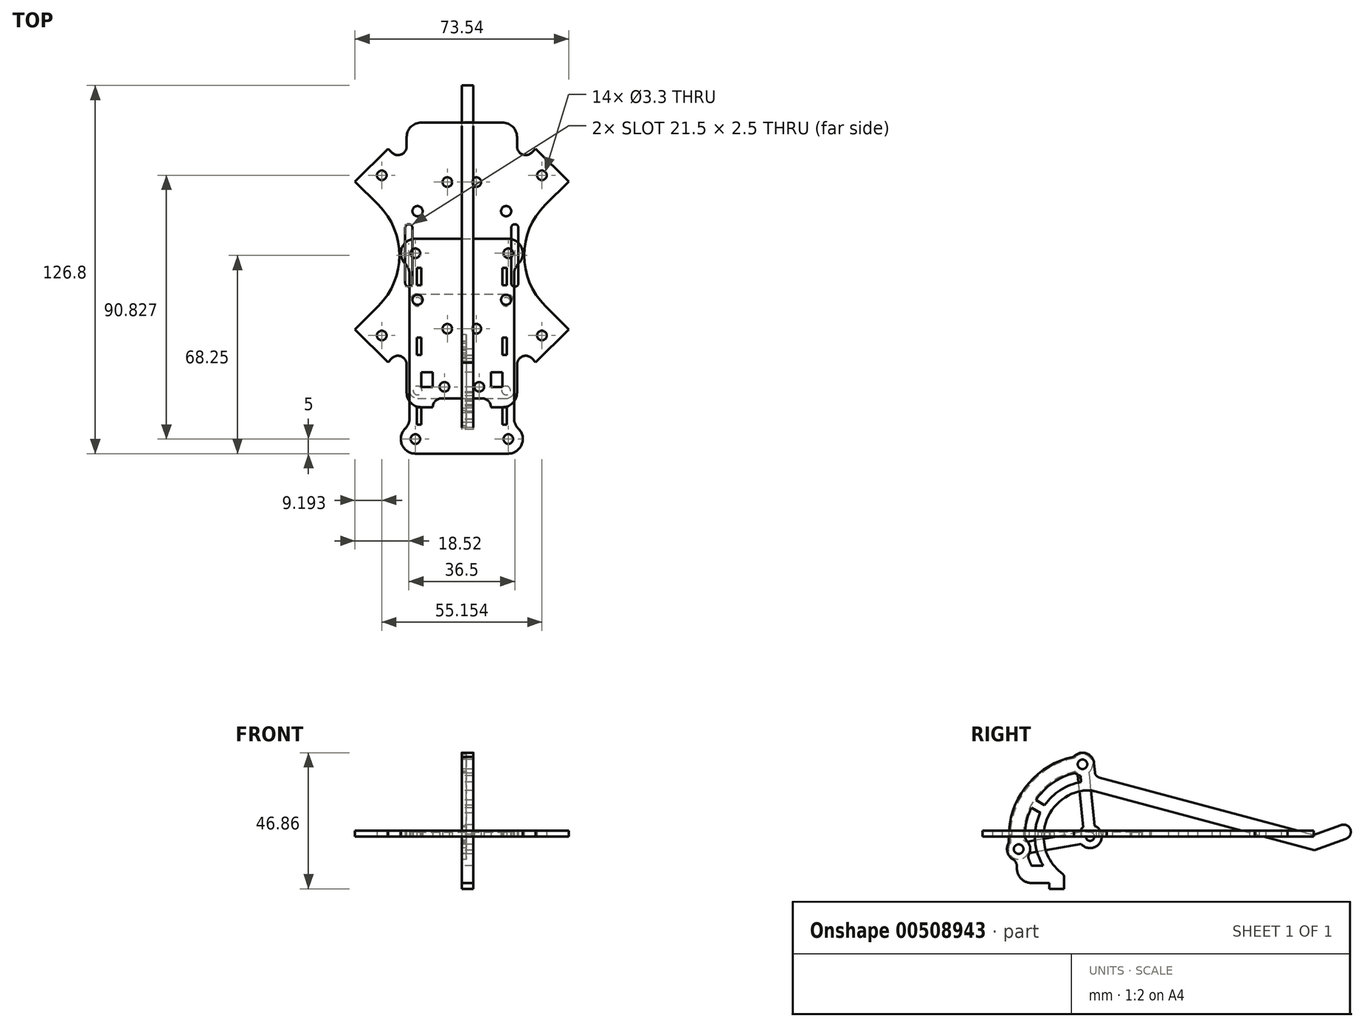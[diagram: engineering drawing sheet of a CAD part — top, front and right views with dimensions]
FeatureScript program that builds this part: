
annotation { "Feature Type Name" : "Feature", "Feature Type Description" : "" }
export const myFeature = defineFeature(function(context is Context, id is Id, definition is map)
    precondition{}
    {
        {
            var Q0;
            Q0=qCreatedBy(makeId("Right.planeOp"),FACE);
            var sketch = newSketch(context, id + "F0", { "sketchPlane" : qUnion([Q0])});
            skCircle(sketch, "E0", {"center": v(0, 0) * mm, "radius": 1.5 * mm, "construction": true});
            skArc(sketch, "E1", {"start": v(-5.7, 27.42) * mm, "mid": v(-22.11, 17.18) * mm, "end": v(-27.97, -1.26) * mm});
            skArc(sketch, "E2", {"start": v(-5.27, 21.87) * mm, "mid": v(-12.86, 18.46) * mm, "end": v(-18.7, 12.52) * mm});
            skLineSegment(sketch, "E3", {"start": v(0, 0) * mm, "end": v(-24.25, 14) * mm, "construction": true});
            skLineSegment(sketch, "E4", {"start": v(0, 0) * mm, "end": v(-60.65, 0) * mm, "construction": true});
            skLineSegment(sketch, "E5", {"start": v(0, 0) * mm, "end": v(-14.34, 20.48) * mm, "construction": true});
            skCircle(sketch, "E6", {"center": v(0, 0) * mm, "radius": 14 * mm, "construction": true});
            skLineSegment(sketch, "E7", {"start": v(-20.16, -10) * mm, "end": v(-16.16, -10) * mm});
            skArc(sketch, "E8", {"start": v(-12.49, -10) * mm, "mid": v(-11.05, -11.57) * mm, "end": v(-9.41, -12.94) * mm});
            skLineSegment(sketch, "E9.trimOffspring", {"start": v(-9, -16) * mm, "end": v(-9, -16) * mm});
            skPoint(sketch, "E10.visualSharp", {"position": v(-20.16, -10) * mm});
            skPoint(sketch, "E11.visualSharp", {"position": v(-22.98, -16) * mm});
            skArc(sketch, "E11.filletArc", {"start": v(-25.18, -10.6) * mm, "mid": v(-23.87, -14.4) * mm, "end": v(-20.2, -16) * mm});
            skLineSegment(sketch, "E12", {"start": v(-14, -16) * mm, "end": v(-14, -18) * mm});
            skLineSegment(sketch, "E13", {"start": v(-14, -18) * mm, "end": v(-9, -18) * mm});
            skLineSegment(sketch, "E14", {"start": v(-9, -18) * mm, "end": v(-9, -16) * mm});
            skLineSegment(sketch, "E15.trimOffspring", {"start": v(-14, -16) * mm, "end": v(-20.2, -16) * mm});
            skLineSegment(sketch, "E16", {"start": v(-9, -13.75) * mm, "end": v(-9, -16) * mm});
            skCircle(sketch, "E17", {"center": v(-24.62, -4.34) * mm, "radius": 1.65 * mm});
            skLineSegment(sketch, "E18", {"start": v(-24.62, -4.34) * mm, "end": v(0, 0) * mm, "construction": true});
            skArc(sketch, "E19", {"start": v(-28.25, -2.66) * mm, "mid": v(-28.44, -5.53) * mm, "end": v(-26.65, -7.79) * mm});
            skArc(sketch, "E20.trimOffspring", {"start": v(-21.45, -6.78) * mm, "mid": v(-20.62, -4.16) * mm, "end": v(-21.7, -1.62) * mm});
            skPoint(sketch, "E21.visualSharp", {"position": v(-27.92, -2.08) * mm});
            skArc(sketch, "E21.filletArc", {"start": v(-28.25, -2.66) * mm, "mid": v(-28.03, -1.97) * mm, "end": v(-27.97, -1.26) * mm});
            skArc(sketch, "E22.filletArc", {"start": v(-22.5, 0.5) * mm, "mid": v(-22.3, -0.64) * mm, "end": v(-21.7, -1.62) * mm});
            skPoint(sketch, "E23.visualSharp", {"position": v(-24.43, -8.34) * mm});
            skArc(sketch, "E23.filletArc", {"start": v(-25.18, -10.6) * mm, "mid": v(-25.51, -8.99) * mm, "end": v(-26.65, -7.79) * mm});
            skPoint(sketch, "E24.visualSharp", {"position": v(-12.49, -10) * mm});
            skPoint(sketch, "E25.visualSharp", {"position": v(-9, -13.23) * mm});
            skArc(sketch, "E25.filletArc", {"start": v(-9, -13.75) * mm, "mid": v(-9.1, -13.3) * mm, "end": v(-9.41, -12.94) * mm});
            skCircle(sketch, "E26", {"center": v(-2.61, 24.86) * mm, "radius": 1.65 * mm});
            skLineSegment(sketch, "E27", {"start": v(-2.61, 24.86) * mm, "end": v(0, 0) * mm, "construction": true});
            skLineSegment(sketch, "E28", {"start": v(1.59, 15.57) * mm, "end": v(77.27, -4.7) * mm});
            skLineSegment(sketch, "E29", {"start": v(-9, -16) * mm, "end": v(82.41, -16) * mm, "construction": true});
            skArc(sketch, "E30", {"start": v(-5.27, 21.87) * mm, "mid": v(-4.34, 21.25) * mm, "end": v(-3.27, 20.92) * mm});
            skLineSegment(sketch, "E31.0", {"start": v(3.12, 20.34) * mm, "end": v(75.83, 0.86) * mm});
            skLineSegment(sketch, "E32", {"start": v(1.37, 25.21) * mm, "end": v(1.64, 22.1) * mm});
            skPoint(sketch, "E32.startSnap0", {"position": v(1.37, 25.21) * mm});
            skLineSegment(sketch, "E33.0", {"start": v(-3.27, 20.92) * mm, "end": v(-3.08, 18.75) * mm});
            skPoint(sketch, "E34.visualSharp", {"position": v(1.77, 20.7) * mm});
            skArc(sketch, "E34.filletArc", {"start": v(1.64, 22.1) * mm, "mid": v(2.1, 20.99) * mm, "end": v(3.12, 20.34) * mm});
            skArc(sketch, "E35.trimOffspring", {"start": v(1.37, 25.21) * mm, "mid": v(-1.42, 28.68) * mm, "end": v(-5.7, 27.42) * mm});
            skArc(sketch, "E36", {"start": v(-2.67, 15.78) * mm, "mid": v(-14.95, 5.7) * mm, "end": v(-12.49, -10) * mm});
            skArc(sketch, "E37.0", {"start": v(-3.08, 18.75) * mm, "mid": v(-10.18, 16.04) * mm, "end": v(-15.65, 10.77) * mm});
            skLineSegment(sketch, "E38", {"start": v(78.23, 0.96) * mm, "end": v(86.44, 3.95) * mm});
            skLineSegment(sketch, "E39.0", {"start": v(77.27, -4.7) * mm, "end": v(88.15, -0.75) * mm});
            skArc(sketch, "E40", {"start": v(88.15, -0.75) * mm, "mid": v(89.65, 2.46) * mm, "end": v(86.44, 3.95) * mm});
            skPoint(sketch, "E41.visualSharp", {"position": v(77.05, 0.53) * mm});
            skArc(sketch, "E41.filletArc", {"start": v(75.83, 0.86) * mm, "mid": v(77.04, 0.73) * mm, "end": v(78.23, 0.96) * mm});
            skArc(sketch, "E42", {"start": v(-20.16, -10) * mm, "mid": v(-20.87, -8.42) * mm, "end": v(-21.45, -6.78) * mm});
            skLineSegment(sketch, "E43", {"start": v(-20.2, 9.93) * mm, "end": v(-17.15, 8.17) * mm});
            skLineSegment(sketch, "E44.MirrorCS", {"start": v(-18.7, 12.52) * mm, "end": v(-15.65, 10.77) * mm});
            skArc(sketch, "E45.trimOffspring", {"start": v(-20.2, 9.93) * mm, "mid": v(-21.86, 5.33) * mm, "end": v(-22.5, 0.5) * mm});
            skArc(sketch, "E46.trimOffspring", {"start": v(-17.15, 8.17) * mm, "mid": v(-18.97, -1.04) * mm, "end": v(-16.16, -10) * mm});
            skPoint(sketch, "E47.visualSharp", {"position": v(0, 16) * mm});
            skArc(sketch, "E47.filletArc", {"start": v(1.59, 15.57) * mm, "mid": v(-0.53, 15.9) * mm, "end": v(-2.67, 15.78) * mm});
            skLineSegment(sketch, "E48", {"start": v(8, -11) * mm, "end": v(44, -11) * mm});
            skSolve(sketch);
        }
        {
            var Q0;
            Q0=makeQuery(id+"F0.imprint","IMPRINT",FACE,{"disambiguationData":[TD([[makeQuery(id+"F0.imprint","IMPRINT",EDGE,{"derivedFrom":sQuery(id+"F0.wireOp",EDGE,"E1")}),1.0]])]});
            extrude(context, id + "F1", {"entities" : qUnion([Q0]), "depth" : 4 * mm});
        }
        {
            var Q0;
            Q0=makeQuery(id+"F1.opExtrude","SWEPT_EDGE",EDGE,{"disambiguationData":[OSD([sQuery(id+"F0.wireOp",EDGE,"E10.filletArc"),sQuery(id+"F0.wireOp",EDGE,"E20.trimOffspring")])]});
            fillet(context, id + "F2", {"entities" : qUnion([Q0]), "radius" : 2 * mm, "tangentPropagation" : true, "allowEdgeOverflow" : false});
        }
        {
            var Q0;
            Q0=qCreatedBy(makeId("Right.planeOp"),FACE);
            var sketch = newSketch(context, id + "F3", { "sketchPlane" : qUnion([Q0])});
            skLineSegment(sketch, "E49", {"start": v(0, 0) * mm, "end": v(-2.61, 24.86) * mm, "construction": true});
            skLineSegment(sketch, "E50", {"start": v(0, 0) * mm, "end": v(-24.62, -4.34) * mm, "construction": true});
            skCircle(sketch, "E51", {"center": v(-24.62, -4.34) * mm, "radius": 1.65 * mm});
            skCircle(sketch, "E52", {"center": v(-2.61, 24.86) * mm, "radius": 1.65 * mm});
            skArc(sketch, "E53", {"start": v(-5.12, 22.42) * mm, "mid": v(-4.74, 22.08) * mm, "end": v(-4.3, 21.8) * mm});
            skArc(sketch, "E54", {"start": v(-27.4, -2.23) * mm, "mid": v(-26.42, -7.34) * mm, "end": v(-21.44, -5.81) * mm});
            skArc(sketch, "E55", {"start": v(-27.4, -2.23) * mm, "mid": v(-21.96, 16.55) * mm, "end": v(-5.41, 26.96) * mm});
            skArc(sketch, "E56", {"start": v(-22.97, -1.26) * mm, "mid": v(-18.37, 13.84) * mm, "end": v(-5.12, 22.42) * mm});
            skLineSegment(sketch, "E57.0", {"start": v(1.63, 3.65) * mm, "end": v(-0.32, 22.22) * mm});
            skLineSegment(sketch, "E58.0", {"start": v(-3.06, -2.57) * mm, "end": v(-21.44, -5.81) * mm});
            skLineSegment(sketch, "E59.MirrorCS", {"start": v(-2.35, 3.24) * mm, "end": v(-4.3, 21.8) * mm});
            skArc(sketch, "E60.trimOffspring", {"start": v(-0.32, 22.22) * mm, "mid": v(-0.23, 27.42) * mm, "end": v(-5.41, 26.96) * mm});
            skArc(sketch, "E61.trimOffspring", {"start": v(-22.14, -1.87) * mm, "mid": v(-22.53, -1.53) * mm, "end": v(-22.97, -1.26) * mm});
            skPoint(sketch, "E62.orphan", {"position": v(-1.8, -2.06) * mm});
            skLineSegment(sketch, "E63.trimOffspring", {"start": v(-3.76, 1.37) * mm, "end": v(-22.14, -1.87) * mm});
            skPoint(sketch, "E64.MirrorCS.start.orphan", {"position": v(1.49, 2.3) * mm});
            skArc(sketch, "E65", {"start": v(-3.06, -2.57) * mm, "mid": v(3.2, -2.4) * mm, "end": v(1.63, 3.65) * mm});
            skPoint(sketch, "E66.orphan", {"position": v(2.18, -1.65) * mm});
            skArc(sketch, "E67.trimOffspring", {"start": v(-2.35, 3.24) * mm, "mid": v(-3.2, 2.4) * mm, "end": v(-3.76, 1.37) * mm});
            skCircle(sketch, "E68", {"center": v(0, 0) * mm, "radius": 1.5 * mm});
            skSolve(sketch);
        }
        {
            var Q0;
            Q0 = qSketchRegion(id + "F3", true);
            extrude(context, id + "F4", {"entities" : qUnion([Q0]), "depth" : 1.5 * mm});
        }
        {
            var Q0;
            Q0=qCreatedBy(makeId("Top.planeOp"),FACE);
            var sketch = newSketch(context, id + "F5", { "sketchPlane" : qUnion([Q0])});
            skLineSegment(sketch, "E69.bottom", {"start": v(-14, 77) * mm, "end": v(14, 77) * mm});
            skLineSegment(sketch, "E69.top", {"start": v(-14, -21) * mm, "end": v(-10, -21) * mm});
            skLineSegment(sketch, "E69.left", {"start": v(-19, 72) * mm, "end": v(-19, 68.8) * mm});
            skLineSegment(sketch, "E69.right", {"start": v(19, 72) * mm, "end": v(19, 68.8) * mm});
            skLineSegment(sketch, "E70.bottom", {"start": v(10, -9) * mm, "end": v(14, -9) * mm});
            skLineSegment(sketch, "E70.top", {"start": v(10, -14) * mm, "end": v(14, -14) * mm});
            skLineSegment(sketch, "E70.left", {"start": v(10, -9) * mm, "end": v(10, -14) * mm});
            skLineSegment(sketch, "E70.right", {"start": v(14, -9) * mm, "end": v(14, -14) * mm});
            skLineSegment(sketch, "E71.MirrorCS", {"start": v(-10, -9) * mm, "end": v(-10, -14) * mm});
            skLineSegment(sketch, "E72.MirrorCS", {"start": v(-10, -9) * mm, "end": v(-14, -9) * mm});
            skLineSegment(sketch, "E73.MirrorCS", {"start": v(-10, -14) * mm, "end": v(-14, -14) * mm});
            skLineSegment(sketch, "E74.MirrorCS", {"start": v(-14, -9) * mm, "end": v(-14, -14) * mm});
            skCircle(sketch, "E75", {"center": v(-6, -14) * mm, "radius": 1.65 * mm});
            skCircle(sketch, "E76.MirrorC", {"center": v(6, -14) * mm, "radius": 1.65 * mm});
            skLineSegment(sketch, "E77", {"start": v(-7, -18) * mm, "end": v(7, -18) * mm});
            skLineSegment(sketch, "E78", {"start": v(10, -21) * mm, "end": v(10, -21) * mm});
            skLineSegment(sketch, "E79", {"start": v(-10, -21) * mm, "end": v(-10, -21) * mm});
            skLineSegment(sketch, "E80.trimOffspring", {"start": v(10, -21) * mm, "end": v(14, -21) * mm});
            skCircle(sketch, "E81", {"center": v(15.25, 16) * mm, "radius": 1.75 * mm});
            skCircle(sketch, "E82", {"center": v(15.25, 46.5) * mm, "radius": 1.75 * mm});
            skCircle(sketch, "E83.MirrorC", {"center": v(-15.25, 46.5) * mm, "radius": 1.75 * mm});
            skCircle(sketch, "E84.MirrorC", {"center": v(-15.25, 16) * mm, "radius": 1.75 * mm});
            skLineSegment(sketch, "E85", {"start": v(0, 31.25) * mm, "end": v(-74.25, -43) * mm, "construction": true});
            skLineSegment(sketch, "E86", {"start": v(0, 31.25) * mm, "end": v(-74.25, 105.5) * mm, "construction": true});
            skLineSegment(sketch, "E87.MirrorCS", {"start": v(0, 31.25) * mm, "end": v(74.25, 105.5) * mm, "construction": true});
            skLineSegment(sketch, "E88.MirrorCS", {"start": v(0, 31.25) * mm, "end": v(74.25, -43) * mm, "construction": true});
            skLineSegment(sketch, "E89", {"start": v(-28.7, 13.86) * mm, "end": v(-36.77, 5.8) * mm});
            skLineSegment(sketch, "E90.MirrorCS", {"start": v(-24.12, -4.19) * mm, "end": v(-25.46, -5.52) * mm});
            skLineSegment(sketch, "E91", {"start": v(-25.46, -5.52) * mm, "end": v(-36.77, 5.8) * mm});
            skLineSegment(sketch, "E92.trimOffspring", {"start": v(-19, -6.3) * mm, "end": v(-19, -16) * mm});
            skLineSegment(sketch, "E93.MirrorCS", {"start": v(28.7, 13.86) * mm, "end": v(36.77, 5.8) * mm});
            skLineSegment(sketch, "E94.MirrorCS", {"start": v(25.46, -5.52) * mm, "end": v(36.77, 5.8) * mm});
            skLineSegment(sketch, "E95.MirrorCS", {"start": v(24.12, -4.19) * mm, "end": v(25.46, -5.52) * mm});
            skLineSegment(sketch, "E96.trimOffspring", {"start": v(19, -6.3) * mm, "end": v(19, -16) * mm});
            skLineSegment(sketch, "E97", {"start": v(0, 31.25) * mm, "end": v(-50, 31.25) * mm, "construction": true});
            skLineSegment(sketch, "E98.MirrorCS", {"start": v(-28.7, 48.64) * mm, "end": v(-36.77, 56.7) * mm});
            skLineSegment(sketch, "E99.MirrorCS", {"start": v(-24.12, 66.69) * mm, "end": v(-25.46, 68.02) * mm});
            skLineSegment(sketch, "E100.MirrorCS", {"start": v(-25.46, 68.02) * mm, "end": v(-36.77, 56.7) * mm});
            skLineSegment(sketch, "E101.MirrorCS", {"start": v(28.7, 48.64) * mm, "end": v(36.77, 56.7) * mm});
            skLineSegment(sketch, "E102.MirrorCS", {"start": v(25.46, 68.02) * mm, "end": v(36.77, 56.7) * mm});
            skLineSegment(sketch, "E103.MirrorCS", {"start": v(24.12, 66.69) * mm, "end": v(25.46, 68.02) * mm});
            skArc(sketch, "E104", {"start": v(-28.7, 13.86) * mm, "mid": v(-21.5, 31.25) * mm, "end": v(-28.7, 48.64) * mm});
            skArc(sketch, "E105.MirrorCS", {"start": v(28.7, 13.86) * mm, "mid": v(21.5, 31.25) * mm, "end": v(28.7, 48.64) * mm});
            skLineSegment(sketch, "E106", {"start": v(-18.25, 40.75) * mm, "end": v(-18.25, 21.75) * mm, "construction": true});
            skArc(sketch, "E107.0.startCap", {"start": v(-19.5, 40.75) * mm, "mid": v(-18.25, 42) * mm, "end": v(-17, 40.75) * mm});
            skArc(sketch, "E107.0.endCap", {"start": v(-17, 21.75) * mm, "mid": v(-18.25, 20.5) * mm, "end": v(-19.5, 21.75) * mm});
            skLineSegment(sketch, "E107.0.left", {"start": v(-17, 40.75) * mm, "end": v(-17, 21.75) * mm});
            skLineSegment(sketch, "E107.0.right", {"start": v(-19.5, 40.75) * mm, "end": v(-19.5, 21.75) * mm});
            skArc(sketch, "E108.MirrorCS", {"start": v(19.5, 40.75) * mm, "mid": v(18.25, 42) * mm, "end": v(17, 40.75) * mm});
            skLineSegment(sketch, "E109.MirrorCS", {"start": v(19.5, 40.75) * mm, "end": v(19.5, 21.75) * mm});
            skLineSegment(sketch, "E110.MirrorCS", {"start": v(17, 40.75) * mm, "end": v(17, 21.75) * mm});
            skArc(sketch, "E111.MirrorCS", {"start": v(17, 21.75) * mm, "mid": v(18.25, 20.5) * mm, "end": v(19.5, 21.75) * mm});
            skPoint(sketch, "E112.visualSharp", {"position": v(-19, 61.56) * mm});
            skPoint(sketch, "E113.visualSharp", {"position": v(-19, 0.94) * mm});
            skPoint(sketch, "E114.visualSharp", {"position": v(19, 0.94) * mm});
            skPoint(sketch, "E115.visualSharp", {"position": v(19, 61.56) * mm});
            skPoint(sketch, "E116.visualSharp", {"position": v(-19, -21) * mm});
            skArc(sketch, "E116.filletArc", {"start": v(-19, -16) * mm, "mid": v(-17.54, -19.54) * mm, "end": v(-14, -21) * mm});
            skPoint(sketch, "E117.visualSharp", {"position": v(19, -21) * mm});
            skArc(sketch, "E117.filletArc", {"start": v(14, -21) * mm, "mid": v(17.54, -19.54) * mm, "end": v(19, -16) * mm});
            skPoint(sketch, "E118.visualSharp", {"position": v(-10, -18) * mm});
            skArc(sketch, "E118.filletArc", {"start": v(-7, -18) * mm, "mid": v(-9.12, -18.88) * mm, "end": v(-10, -21) * mm});
            skPoint(sketch, "E119.visualSharp", {"position": v(10, -18) * mm});
            skArc(sketch, "E119.filletArc", {"start": v(10, -21) * mm, "mid": v(9.12, -18.88) * mm, "end": v(7, -18) * mm});
            skCircle(sketch, "E120", {"center": v(-27.58, 3.67) * mm, "radius": 1.65 * mm});
            skCircle(sketch, "E121.MirrorC", {"center": v(27.58, 3.67) * mm, "radius": 1.65 * mm});
            skCircle(sketch, "E122.MirrorC", {"center": v(-27.58, 58.83) * mm, "radius": 1.65 * mm});
            skCircle(sketch, "E123.MirrorC", {"center": v(27.58, 58.83) * mm, "radius": 1.65 * mm});
            skCircle(sketch, "E124", {"center": v(-5, 6) * mm, "radius": 1.65 * mm});
            skCircle(sketch, "E125.MirrorC", {"center": v(5, 6) * mm, "radius": 1.65 * mm});
            skCircle(sketch, "E126.MirrorC", {"center": v(-5, 56.5) * mm, "radius": 1.65 * mm});
            skCircle(sketch, "E127.MirrorC", {"center": v(5, 56.5) * mm, "radius": 1.65 * mm});
            skArc(sketch, "E128.filletArc", {"start": v(-19, -6.3) * mm, "mid": v(-20.85, -3.53) * mm, "end": v(-24.12, -4.19) * mm});
            skArc(sketch, "E129.filletArc", {"start": v(24.12, -4.19) * mm, "mid": v(20.85, -3.53) * mm, "end": v(19, -6.3) * mm});
            skArc(sketch, "E130.filletArc", {"start": v(-24.12, 66.69) * mm, "mid": v(-20.85, 66.03) * mm, "end": v(-19, 68.8) * mm});
            skArc(sketch, "E131.filletArc", {"start": v(19, 68.8) * mm, "mid": v(20.85, 66.03) * mm, "end": v(24.12, 66.69) * mm});
            skPoint(sketch, "E132.visualSharp", {"position": v(-19, 77) * mm});
            skArc(sketch, "E132.filletArc", {"start": v(-14, 77) * mm, "mid": v(-17.54, 75.54) * mm, "end": v(-19, 72) * mm});
            skPoint(sketch, "E133.visualSharp", {"position": v(19, 77) * mm});
            skArc(sketch, "E133.filletArc", {"start": v(19, 72) * mm, "mid": v(17.54, 75.54) * mm, "end": v(14, 77) * mm});
            skSolve(sketch);
        }
        {
            var Q0;
            Q0=makeQuery(id+"F5.imprint","IMPRINT",FACE,{"disambiguationData":[TD([[makeQuery(id+"F5.imprint","IMPRINT",EDGE,{"derivedFrom":sQuery(id+"F5.wireOp",EDGE,"E69.bottom")}),-1.0]])]});
            extrude(context, id + "F6", {"entities" : qUnion([Q0]), "depth" : 2 * mm});
        }
        {
            var Q0;
            Q0=qCreatedBy(makeId("Top.planeOp"),FACE);
            var sketch = newSketch(context, id + "F7", { "sketchPlane" : qUnion([Q0])});
            skLineSegment(sketch, "E134.bottom", {"start": v(-15.25, 18) * mm, "end": v(15.25, 18) * mm});
            skLineSegment(sketch, "E134.top", {"start": v(-15.25, -18) * mm, "end": v(15.25, -18) * mm});
            skLineSegment(sketch, "E134.left", {"start": v(-18, 15.25) * mm, "end": v(-18, -15.25) * mm});
            skLineSegment(sketch, "E134.right", {"start": v(18, 15.25) * mm, "end": v(18, -15.25) * mm});
            skPoint(sketch, "E135.visualSharp", {"position": v(-18, 18) * mm});
            skArc(sketch, "E135.filletArc", {"start": v(-15.25, 18) * mm, "mid": v(-17.2, 17.2) * mm, "end": v(-18, 15.25) * mm});
            skPoint(sketch, "E136.visualSharp", {"position": v(18, 18) * mm});
            skArc(sketch, "E136.filletArc", {"start": v(18, 15.25) * mm, "mid": v(17.2, 17.2) * mm, "end": v(15.25, 18) * mm});
            skPoint(sketch, "E137.visualSharp", {"position": v(18, -18) * mm});
            skArc(sketch, "E137.filletArc", {"start": v(15.25, -18) * mm, "mid": v(17.2, -17.2) * mm, "end": v(18, -15.25) * mm});
            skPoint(sketch, "E138.visualSharp", {"position": v(-18, -18) * mm});
            skArc(sketch, "E138.filletArc", {"start": v(-18, -15.25) * mm, "mid": v(-17.2, -17.2) * mm, "end": v(-15.25, -18) * mm});
            skCircle(sketch, "E139", {"center": v(-15.25, 15.25) * mm, "radius": 1.5 * mm});
            skCircle(sketch, "E140", {"center": v(15.25, 15.25) * mm, "radius": 1.5 * mm});
            skCircle(sketch, "E141", {"center": v(15.25, -15.25) * mm, "radius": 1.5 * mm});
            skCircle(sketch, "E142", {"center": v(-15.25, -15.25) * mm, "radius": 1.5 * mm});
            skSolve(sketch);
        }
        {
            var Q0;
            Q0=makeQuery(id+"F7.imprint","IMPRINT",FACE,{"disambiguationData":[TD([[makeQuery(id+"F7.imprint","IMPRINT",EDGE,{"derivedFrom":sQuery(id+"F7.wireOp",EDGE,"E134.bottom")}),-1.0]])]});
            extrude(context, id + "F8", {"entities" : qUnion([Q0]), "depth" : 1.5 * mm});
        }
        {
            var Q0;
            Q0=qCreatedBy(makeId("Top.planeOp"),FACE);
            var sketch = newSketch(context, id + "F9", { "sketchPlane" : qUnion([Q0])});
            skLineSegment(sketch, "E143.bottom", {"start": v(-16, 37) * mm, "end": v(16, 37) * mm});
            skLineSegment(sketch, "E143.top", {"start": v(-16, -37) * mm, "end": v(16, -37) * mm});
            skLineSegment(sketch, "E144.bottom", {"start": v(-15.5, 27) * mm, "end": v(-14, 27) * mm});
            skLineSegment(sketch, "E144.top", {"start": v(-15.5, 21) * mm, "end": v(-14, 21) * mm});
            skLineSegment(sketch, "E144.left", {"start": v(-15.5, 27) * mm, "end": v(-15.5, 21) * mm});
            skLineSegment(sketch, "E144.right", {"start": v(-14, 27) * mm, "end": v(-14, 21) * mm});
            skLineSegment(sketch, "E145.bottom", {"start": v(-15.5, 3) * mm, "end": v(-14, 3) * mm});
            skLineSegment(sketch, "E145.top", {"start": v(-15.5, -3) * mm, "end": v(-14, -3) * mm});
            skLineSegment(sketch, "E145.left", {"start": v(-15.5, 3) * mm, "end": v(-15.5, -3) * mm});
            skLineSegment(sketch, "E145.right", {"start": v(-14, 3) * mm, "end": v(-14, -3) * mm});
            skLineSegment(sketch, "E146.MirrorCS", {"start": v(-15.5, -27) * mm, "end": v(-14, -27) * mm});
            skLineSegment(sketch, "E147.MirrorCS", {"start": v(-15.5, -21) * mm, "end": v(-14, -21) * mm});
            skLineSegment(sketch, "E148.MirrorCS", {"start": v(-15.5, -27) * mm, "end": v(-15.5, -21) * mm});
            skLineSegment(sketch, "E149.MirrorCS", {"start": v(-14, -27) * mm, "end": v(-14, -21) * mm});
            skLineSegment(sketch, "E150.MirrorCS", {"start": v(15.5, -27) * mm, "end": v(14, -27) * mm});
            skLineSegment(sketch, "E151.MirrorCS", {"start": v(15.5, -3) * mm, "end": v(14, -3) * mm});
            skLineSegment(sketch, "E152.MirrorCS", {"start": v(15.5, 3) * mm, "end": v(14, 3) * mm});
            skLineSegment(sketch, "E153.MirrorCS", {"start": v(15.5, 27) * mm, "end": v(14, 27) * mm});
            skLineSegment(sketch, "E154.MirrorCS", {"start": v(15.5, -21) * mm, "end": v(14, -21) * mm});
            skLineSegment(sketch, "E155.MirrorCS", {"start": v(15.5, 21) * mm, "end": v(14, 21) * mm});
            skLineSegment(sketch, "E156.MirrorCS", {"start": v(15.5, -27) * mm, "end": v(15.5, -21) * mm});
            skLineSegment(sketch, "E157.MirrorCS", {"start": v(14, 3) * mm, "end": v(14, -3) * mm});
            skLineSegment(sketch, "E158.MirrorCS", {"start": v(15.5, 3) * mm, "end": v(15.5, -3) * mm});
            skLineSegment(sketch, "E159.MirrorCS", {"start": v(14, -27) * mm, "end": v(14, -21) * mm});
            skLineSegment(sketch, "E160.MirrorCS", {"start": v(14, 27) * mm, "end": v(14, 21) * mm});
            skLineSegment(sketch, "E161.MirrorCS", {"start": v(15.5, 27) * mm, "end": v(15.5, 21) * mm});
            skCircle(sketch, "E162", {"center": v(-16, 32) * mm, "radius": 1.65 * mm});
            skLineSegment(sketch, "E163.trimOffspring", {"start": v(-18, 24.86) * mm, "end": v(-18, -24.86) * mm});
            skCircle(sketch, "E164.MirrorC", {"center": v(16, 32) * mm, "radius": 1.65 * mm});
            skLineSegment(sketch, "E165.trimOffspring", {"start": v(18, 24.86) * mm, "end": v(18, -24.86) * mm});
            skCircle(sketch, "E166.MirrorC", {"center": v(-16, -32) * mm, "radius": 1.65 * mm});
            skCircle(sketch, "E167.MirrorC", {"center": v(16, -32) * mm, "radius": 1.65 * mm});
            skArc(sketch, "E168.MirrorCS", {"start": v(16, -37) * mm, "mid": v(20.63, -33.9) * mm, "end": v(19.5, -28.43) * mm});
            skArc(sketch, "E169.MirrorCS", {"start": v(-16, -37) * mm, "mid": v(-20.63, -33.9) * mm, "end": v(-19.5, -28.43) * mm});
            skArc(sketch, "E170", {"start": v(-16, 37) * mm, "mid": v(-20.63, 33.9) * mm, "end": v(-19.5, 28.43) * mm});
            skArc(sketch, "E171.MirrorCS", {"start": v(16, 37) * mm, "mid": v(20.63, 33.9) * mm, "end": v(19.5, 28.43) * mm});
            skPoint(sketch, "E172.visualSharp", {"position": v(18, -27.42) * mm});
            skArc(sketch, "E172.filletArc", {"start": v(18, -24.86) * mm, "mid": v(18.4, -26.8) * mm, "end": v(19.5, -28.43) * mm});
            skPoint(sketch, "E173.visualSharp", {"position": v(-18, -27.42) * mm});
            skArc(sketch, "E173.filletArc", {"start": v(-19.5, -28.43) * mm, "mid": v(-18.4, -26.8) * mm, "end": v(-18, -24.86) * mm});
            skPoint(sketch, "E174.visualSharp", {"position": v(-18, 27.42) * mm});
            skArc(sketch, "E174.filletArc", {"start": v(-18, 24.86) * mm, "mid": v(-18.4, 26.8) * mm, "end": v(-19.5, 28.43) * mm});
            skPoint(sketch, "E175.visualSharp", {"position": v(18, 27.42) * mm});
            skArc(sketch, "E175.filletArc", {"start": v(19.5, 28.43) * mm, "mid": v(18.4, 26.8) * mm, "end": v(18, 24.86) * mm});
            skSolve(sketch);
        }
        {
            var Q0;
            Q0=makeQuery(id+"F9.imprint","IMPRINT",FACE,{"disambiguationData":[TD([[makeQuery(id+"F9.imprint","IMPRINT",EDGE,{"derivedFrom":sQuery(id+"F9.wireOp",EDGE,"E143.bottom")}),-1.0]])]});
            extrude(context, id + "F10", {"entities" : qUnion([Q0]), "depth" : 2 * mm});
        }
    });
